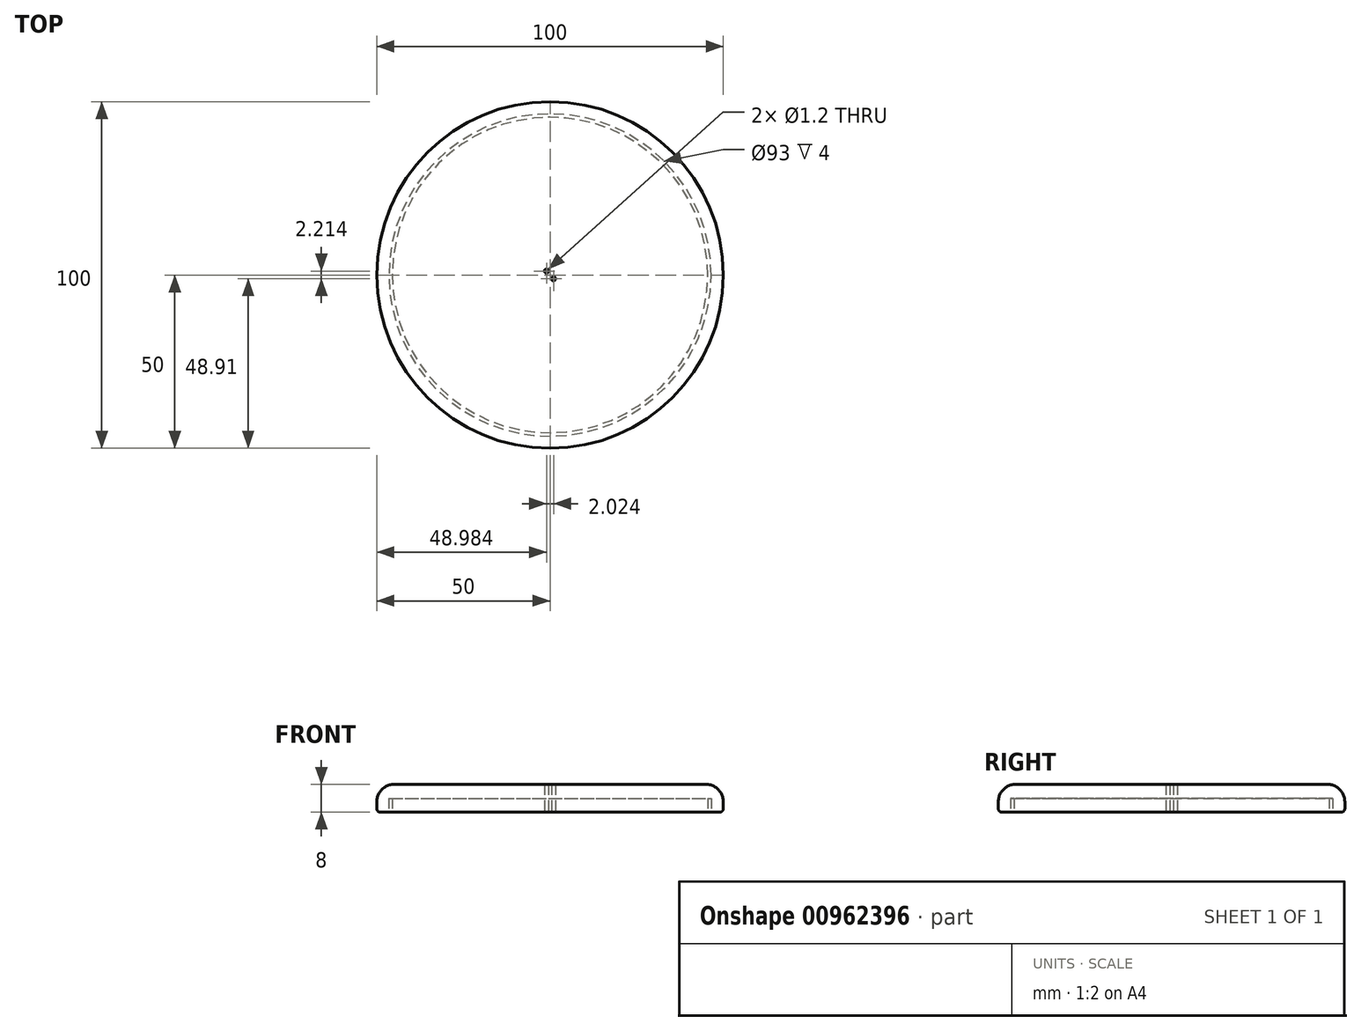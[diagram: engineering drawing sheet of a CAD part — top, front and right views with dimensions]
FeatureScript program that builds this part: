
annotation { "Feature Type Name" : "Feature", "Feature Type Description" : "" }
export const myFeature = defineFeature(function(context is Context, id is Id, definition is map)
    precondition{}
    {
        {
            var Q0;
            Q0=qCreatedBy(makeId("Top.planeOp"),FACE);
            var sketch = newSketch(context, id + "F0", { "sketchPlane" : qUnion([Q0])});
            skCircle(sketch, "E0", {"center": v(0, 0) * mm, "radius": 50 * mm});
            skCircle(sketch, "E1", {"center": v(-1.02, 1.12) * mm, "radius": 0.6 * mm});
            skCircle(sketch, "E2", {"center": v(1, -1.1) * mm, "radius": 0.6 * mm});
            skSolve(sketch);
        }
        {
            var Q0;
            Q0=makeQuery(id+"F0.imprint","IMPRINT",FACE,{"disambiguationData":[TD([[makeQuery(id+"F0.imprint","IMPRINT",EDGE,{"derivedFrom":sQuery(id+"F0.wireOp",EDGE,"E0")}),1.0]])]});
            extrude(context, id + "F1", {"entities" : qUnion([Q0]), "depth" : 8 * mm, "offsetDistance" : 25 * mm});
        }
        {
            var Q0;
            Q0=makeQuery(id+"F1.opExtrude","CAP_EDGE",EDGE,{"disambiguationData":[OSD([sQuery(id+"F0.wireOp",EDGE,"E0")])],"isStart":false});
            fillet(context, id + "F2", {"entities" : qUnion([Q0]), "radius" : 5 * mm, "tangentPropagation" : true, "allowEdgeOverflow" : false});
        }
        {
            var Q0;
            Q0=makeQuery(id+"F1.opExtrude","CAP_EDGE",EDGE,{"disambiguationData":[OSD([sQuery(id+"F0.wireOp",EDGE,"E0")])],"isStart":true});
            fillet(context, id + "F3", {"entities" : qUnion([Q0]), "radius" : 1 * mm, "tangentPropagation" : true, "allowEdgeOverflow" : false});
        }
        {
            var Q0;
            Q0=makeQuery(id+"F1.opExtrude","CAP_FACE",FACE,{"disambiguationData":[OSD([sQuery(id+"F0.wireOp",EDGE,"E0"),sQuery(id+"F0.wireOp",EDGE,"E1"),sQuery(id+"F0.wireOp",EDGE,"E2")])],"isStart":true});
            var sketch = newSketch(context, id + "F4", { "sketchPlane" : qUnion([Q0])});
            skCircle(sketch, "E3", {"center": v(0, 0) * mm, "radius": 46.5 * mm});
            skCircle(sketch, "E4", {"center": v(0, 0) * mm, "radius": 45.5 * mm});
            skSolve(sketch);
        }
        {
            var Q0;
            Q0=makeQuery(id+"F4.imprint","IMPRINT",FACE,{"disambiguationData":[TD([[makeQuery(id+"F4.imprint","IMPRINT",EDGE,{"derivedFrom":sQuery(id+"F4.wireOp",EDGE,"E3")}),1.0]])]});
            extrude(context, id + "F5", {"entities" : qUnion([Q0]), "operationType" : NewBodyOperationType.REMOVE, "oppositeDirection" : true, "depth" : 4 * mm, "offsetDistance" : 25 * mm});
        }
    });
